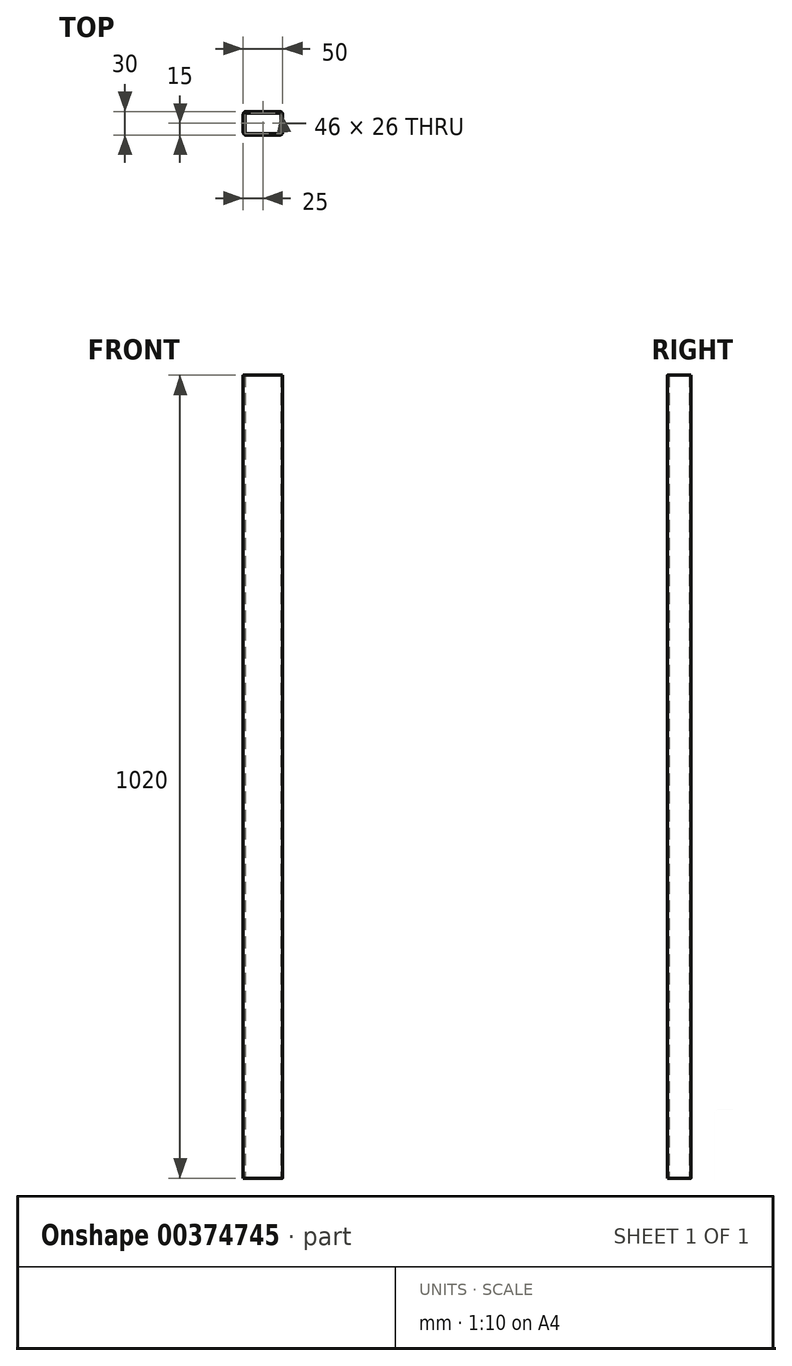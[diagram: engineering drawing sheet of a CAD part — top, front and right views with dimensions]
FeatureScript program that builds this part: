
annotation { "Feature Type Name" : "Feature", "Feature Type Description" : "" }
export const myFeature = defineFeature(function(context is Context, id is Id, definition is map)
    precondition{}
    {
        {
            var Q0;
            Q0=qCreatedBy(makeId("Top.planeOp"),FACE);
            var sketch = newSketch(context, id + "F0", { "sketchPlane" : qUnion([Q0])});
            skLineSegment(sketch, "E0.bottom", {"start": v(21.5, 15) * mm, "end": v(-21.5, 15) * mm});
            skLineSegment(sketch, "E0.top", {"start": v(21.5, -15) * mm, "end": v(-21.5, -15) * mm});
            skLineSegment(sketch, "E0.left", {"start": v(25, 11.5) * mm, "end": v(25, -11.5) * mm});
            skLineSegment(sketch, "E0.right", {"start": v(-25, 11.5) * mm, "end": v(-25, -11.5) * mm});
            skPoint(sketch, "E0.middle", {"position": v(0, 0) * mm});
            skLineSegment(sketch, "E1.bottom", {"start": v(23, -13) * mm, "end": v(-23, -13) * mm});
            skLineSegment(sketch, "E1.top", {"start": v(23, 13) * mm, "end": v(-23, 13) * mm});
            skLineSegment(sketch, "E1.left", {"start": v(23, -13) * mm, "end": v(23, 13) * mm});
            skLineSegment(sketch, "E1.right", {"start": v(-23, -13) * mm, "end": v(-23, 13) * mm});
            skPoint(sketch, "E2.visualSharp", {"position": v(-25, 15) * mm});
            skArc(sketch, "E2.filletArc", {"start": v(-21.5, 15) * mm, "mid": v(-23.97, 13.97) * mm, "end": v(-25, 11.5) * mm});
            skPoint(sketch, "E3.visualSharp", {"position": v(-25, -15) * mm});
            skArc(sketch, "E3.filletArc", {"start": v(-25, -11.5) * mm, "mid": v(-23.97, -13.97) * mm, "end": v(-21.5, -15) * mm});
            skPoint(sketch, "E4.visualSharp", {"position": v(25, -15) * mm});
            skArc(sketch, "E4.filletArc", {"start": v(21.5, -15) * mm, "mid": v(23.97, -13.97) * mm, "end": v(25, -11.5) * mm});
            skPoint(sketch, "E5.visualSharp", {"position": v(25, 15) * mm});
            skArc(sketch, "E5.filletArc", {"start": v(25, 11.5) * mm, "mid": v(23.97, 13.97) * mm, "end": v(21.5, 15) * mm});
            skSolve(sketch);
        }
        {
            var Q0;
            Q0=makeQuery(id+"F0.imprint","IMPRINT",FACE,{"disambiguationData":[TD([[makeQuery(id+"F0.imprint","IMPRINT",EDGE,{"derivedFrom":sQuery(id+"F0.wireOp",EDGE,"E0.bottom")}),1.0]])]});
            extrude(context, id + "F1", {"entities" : qUnion([Q0]), "depth" : 1020 * mm, "offsetDistance" : 25 * mm});
        }
    });
